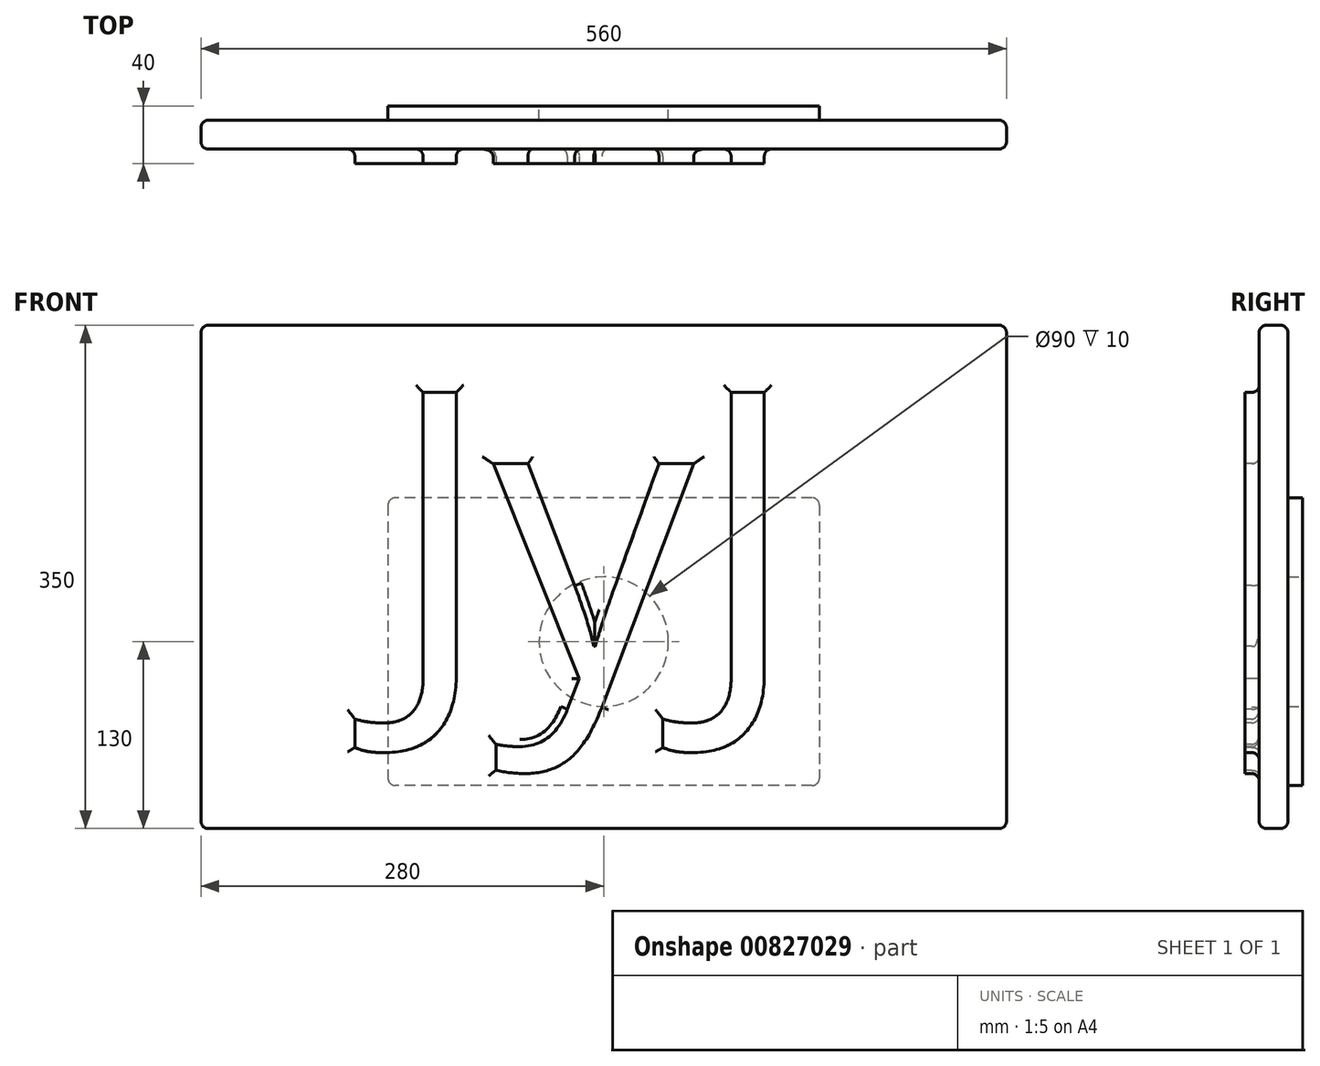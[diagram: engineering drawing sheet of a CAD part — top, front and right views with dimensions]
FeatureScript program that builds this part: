
annotation { "Feature Type Name" : "Feature", "Feature Type Description" : "" }
export const myFeature = defineFeature(function(context is Context, id is Id, definition is map)
    precondition{}
    {
        {
            var Q0;
            Q0=qCreatedBy(makeId("Front.planeOp"),FACE);
            var sketch = newSketch(context, id + "F0", { "sketchPlane" : qUnion([Q0])});
            skLineSegment(sketch, "E0.bottom", {"start": v(-280, 175) * mm, "end": v(280, 175) * mm});
            skLineSegment(sketch, "E0.top", {"start": v(-280, -175) * mm, "end": v(280, -175) * mm});
            skLineSegment(sketch, "E0.left", {"start": v(-280, 175) * mm, "end": v(-280, -175) * mm});
            skLineSegment(sketch, "E0.right", {"start": v(280, 175) * mm, "end": v(280, -175) * mm});
            skLineSegment(sketch, "E1.bottom", {"start": v(150, 55) * mm, "end": v(-150, 55) * mm});
            skLineSegment(sketch, "E1.top", {"start": v(150, -145) * mm, "end": v(-150, -145) * mm});
            skLineSegment(sketch, "E1.left", {"start": v(150, 55) * mm, "end": v(150, -145) * mm});
            skLineSegment(sketch, "E1.right", {"start": v(-150, 55) * mm, "end": v(-150, -145) * mm});
            skSolve(sketch);
        }
        {
            var Q0;
            Q0=makeQuery(id+"F0.imprint","IMPRINT",FACE,{"disambiguationData":[TD([[makeQuery(id+"F0.imprint","IMPRINT",EDGE,{"derivedFrom":sQuery(id+"F0.wireOp",EDGE,"E0.bottom")}),-1.0]])]});
            extrude(context, id + "F1", {"entities" : qUnion([Q0]), "oppositeDirection" : true, "depth" : 20 * mm, "offsetDistance" : 25 * mm});
        }
        {
            var Q0;
            Q0=makeQuery(id+"F0.imprint","IMPRINT",FACE,{"disambiguationData":[TD([[makeQuery(id+"F0.imprint","IMPRINT",EDGE,{"derivedFrom":sQuery(id+"F0.wireOp",EDGE,"E1.bottom")}),1.0]])]});
            extrude(context, id + "F2", {"entities" : qUnion([Q0]), "operationType" : NewBodyOperationType.ADD, "oppositeDirection" : true, "depth" : 30 * mm, "offsetDistance" : 25 * mm});
        }
        {
            var Q0;
            Q0=qCreatedBy(makeId("Front.planeOp"),FACE);
            cPlane(context, id + "F3", {"entities" : qUnion([Q0]), "cplaneType" : CPlaneType.OFFSET, "offset" : 10 * mm, "width" : 150 * mm, "height" : 150 * mm});
        }
        {
            var Q0;
            Q0=qCreatedBy(id+"F3.planeOp",FACE);
            var sketch = newSketch(context, id + "F4", { "sketchPlane" : qUnion([Q0])});
            skText(sketch, "E2", { "text": "JyJ\n", "fontName": "OpenSans-Regular.ttf"});
            const initialGuessF4  = {"E2": [-0.15135, -0.07, 1, 0, 0.2]};
            skSetInitialGuess(sketch, initialGuessF4);
            skSolve(sketch);
        }
        {
            var Q0;
            Q0 = qSketchRegion(id + "F4", true);
            extrude(context, id + "F5", {"entities" : qUnion([Q0]), "operationType" : NewBodyOperationType.ADD, "endBound" : BoundingType.UP_TO_NEXT, "oppositeDirection" : true, "depth" : 25 * mm, "offsetDistance" : 25 * mm});
        }
        {
            var Q0;
            Q0=makeQuery(id+"F1.opExtrude","SWEPT_EDGE",EDGE,{"disambiguationData":[OSD([sQuery(id+"F0.wireOp",EDGE,"E0.bottom"),sQuery(id+"F0.wireOp",EDGE,"E0.right")])]});
            var Q1;
            Q1=makeQuery(id+"F1.opExtrude","SWEPT_EDGE",EDGE,{"disambiguationData":[OSD([sQuery(id+"F0.wireOp",EDGE,"E0.bottom"),sQuery(id+"F0.wireOp",EDGE,"E0.left")])]});
            var Q2;
            Q2=makeQuery(id+"F1.opExtrude","SWEPT_EDGE",EDGE,{"disambiguationData":[OSD([sQuery(id+"F0.wireOp",EDGE,"E0.top"),sQuery(id+"F0.wireOp",EDGE,"E0.left")])]});
            var Q3;
            Q3=makeQuery(id+"F1.opExtrude","SWEPT_EDGE",EDGE,{"disambiguationData":[OSD([sQuery(id+"F0.wireOp",EDGE,"E0.top"),sQuery(id+"F0.wireOp",EDGE,"E0.right")])]});
            var Q4;
            {var subQ0=sQuery(id+"F0.wireOp",EDGE,"E1.right");var subQ1=sQuery(id+"F0.wireOp",EDGE,"E1.left");var subQ2=sQuery(id+"F0.wireOp",EDGE,"E1.top");var subQ3=sQuery(id+"F0.wireOp",EDGE,"E1.bottom");Q4=makeQuery(id+"F2.boolean.opBoolean","MERGE",FACE,{"derivedFrom":[makeQuery(id+"F1.opExtrude","CAP_FACE",FACE,{"disambiguationData":[OSD([sQuery(id+"F0.wireOp",EDGE,"E0.bottom"),sQuery(id+"F0.wireOp",EDGE,"E0.top"),sQuery(id+"F0.wireOp",EDGE,"E0.left"),sQuery(id+"F0.wireOp",EDGE,"E0.right"),subQ3,subQ2,subQ1,subQ0])],"isStart":true}),makeQuery(id+"F2.opExtrude","CAP_FACE",FACE,{"disambiguationData":[OSD([subQ3,subQ2,subQ1,subQ0])],"isStart":true})]});}
            var Q5;
            Q5=makeQuery(id+"F1.opExtrude","CAP_EDGE",EDGE,{"disambiguationData":[OSD([sQuery(id+"F0.wireOp",EDGE,"E0.bottom")])],"isStart":false});
            var Q6;
            Q6=makeQuery(id+"F1.opExtrude","CAP_EDGE",EDGE,{"disambiguationData":[OSD([sQuery(id+"F0.wireOp",EDGE,"E0.right")])],"isStart":false});
            var Q7;
            Q7=makeQuery(id+"F1.opExtrude","CAP_EDGE",EDGE,{"disambiguationData":[OSD([sQuery(id+"F0.wireOp",EDGE,"E0.top")])],"isStart":false});
            var Q8;
            Q8=makeQuery(id+"F1.opExtrude","CAP_EDGE",EDGE,{"disambiguationData":[OSD([sQuery(id+"F0.wireOp",EDGE,"E0.left")])],"isStart":false});
            var Q9;
            Q9=makeQuery(id+"F2.opExtrude","SWEPT_EDGE",EDGE,{"disambiguationData":[OSD([sQuery(id+"F0.wireOp",EDGE,"E1.bottom"),sQuery(id+"F0.wireOp",EDGE,"E1.left")])]});
            var Q10;
            Q10=makeQuery(id+"F2.opExtrude","SWEPT_EDGE",EDGE,{"disambiguationData":[OSD([sQuery(id+"F0.wireOp",EDGE,"E1.bottom"),sQuery(id+"F0.wireOp",EDGE,"E1.right")])]});
            var Q11;
            Q11=makeQuery(id+"F2.opExtrude","SWEPT_EDGE",EDGE,{"disambiguationData":[OSD([sQuery(id+"F0.wireOp",EDGE,"E1.top"),sQuery(id+"F0.wireOp",EDGE,"E1.right")])]});
            var Q12;
            Q12=makeQuery(id+"F2.opExtrude","SWEPT_EDGE",EDGE,{"disambiguationData":[OSD([sQuery(id+"F0.wireOp",EDGE,"E1.top"),sQuery(id+"F0.wireOp",EDGE,"E1.left")])]});
            fillet(context, id + "F6", {"entities" : qUnion([Q0, Q1, Q2, Q3, Q4, Q5, Q6, Q7, Q8, Q9, Q10, Q11, Q12]), "radius" : 5 * mm, "tangentPropagation" : true, "allowEdgeOverflow" : false});
        }
        {
            var Q0;
            Q0=makeQuery(id+"F2.opExtrude","CAP_FACE",FACE,{"disambiguationData":[OSD([sQuery(id+"F0.wireOp",EDGE,"E1.bottom"),sQuery(id+"F0.wireOp",EDGE,"E1.top"),sQuery(id+"F0.wireOp",EDGE,"E1.left"),sQuery(id+"F0.wireOp",EDGE,"E1.right")])],"isStart":false});
            var sketch = newSketch(context, id + "F7", { "sketchPlane" : qUnion([Q0])});
            skCircle(sketch, "E3", {"center": v(0, -45) * mm, "radius": 45 * mm});
            skSolve(sketch);
        }
        {
            var Q0;
            Q0 = qSketchRegion(id + "F7", true);
            extrude(context, id + "F8", {"entities" : qUnion([Q0]), "operationType" : NewBodyOperationType.REMOVE, "oppositeDirection" : true, "depth" : 10 * mm, "offsetDistance" : 25 * mm});
        }
    });
